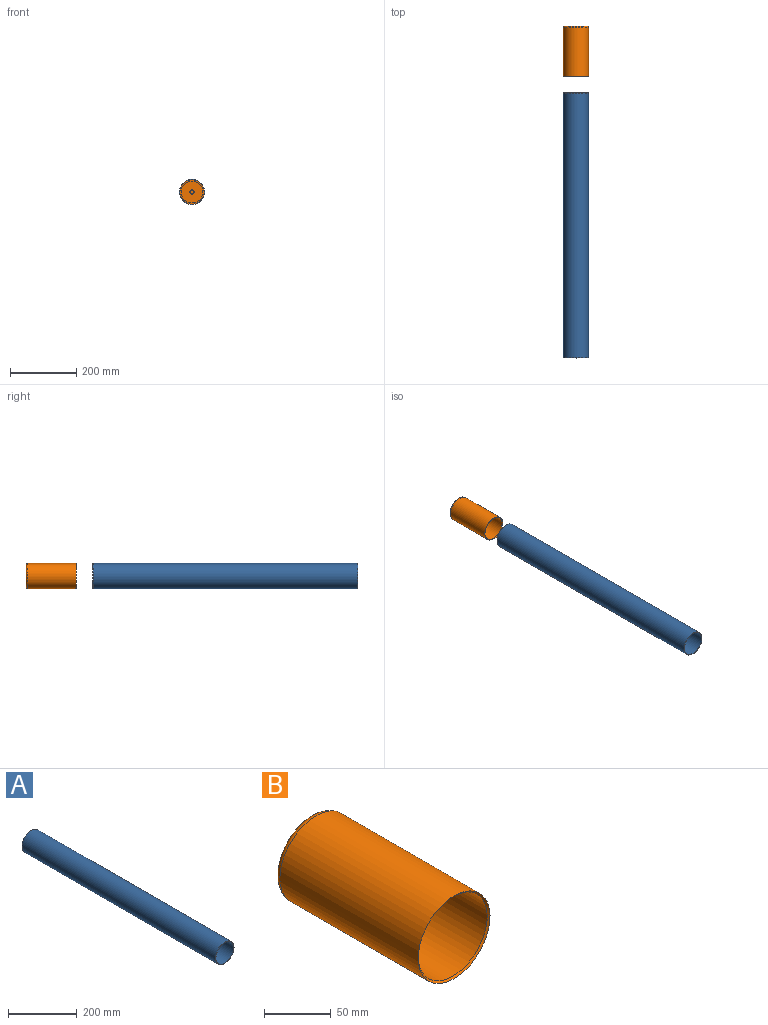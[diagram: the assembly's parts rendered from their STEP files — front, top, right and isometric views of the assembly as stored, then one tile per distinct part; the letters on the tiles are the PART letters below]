
ASSEMBLY  parts=2 mates=1
PART A: 4 faces, bbox 76x798.5x76 mm
  f0: cylinder r=36.5mm len=798.5mm, axis (0,1,0), area 183125mm2, adj f2,f3
  f1: cylinder r=38mm len=797mm, axis (0,1,0), area 190292.6mm2, adj f2,f3
  f2: plane 76x76mm, normal (0,-1,0), area 351.1mm2, adj f0,f1
  f3: cone r=38mm half-angle=45deg, axis (0,-1,0), area 496.5mm2, adj f0,f1
PART B: 10 faces, bbox 82.3x151.5x82.3 mm
  f0: plane 73x73mm, normal (0,-1,0), area 4052.7mm2, adj f3,f5
  f1: cylinder r=38mm len=146.5mm, axis (0,-1,0), area 34978.5mm2, adj f8,f9
  f2: plane 66x66mm, normal (0,1,0), area 3421.2mm2, adj f8
  f3: cylinder r=36.5mm len=147mm, axis (0,1,0), area 33712.4mm2, adj f0,f9
  f4: cylinder r=5mm len=10mm, axis (0,1,0), area 157.1mm2, adj f6,f7
  f5: cylinder r=6.5mm len=13mm, axis (0,1,0), area 204.2mm2, adj f0,f6
  f6: plane 13x13mm, normal (0,-1,0), area 54.2mm2, adj f4,f5
  f7: plane 10x10mm, normal (0,-1,0), area 78.5mm2, adj f4
  f8: torus R=33mm, axis (0,-1,0), area 1785.6mm2, adj f1,f2
  f9: cone r=36.5mm half-angle=45deg, axis (0,-1,0), area 496.5mm2, adj f1,f3
PLACE A t=(-236.23,163.96,-150.61)mm
PLACE B t=(-236.23,360.96,-150.61)mm
MATE planar B.f3 <-> A.f1  axis (0,-1,0) through (-236.23,212.46,-150.61)mm
